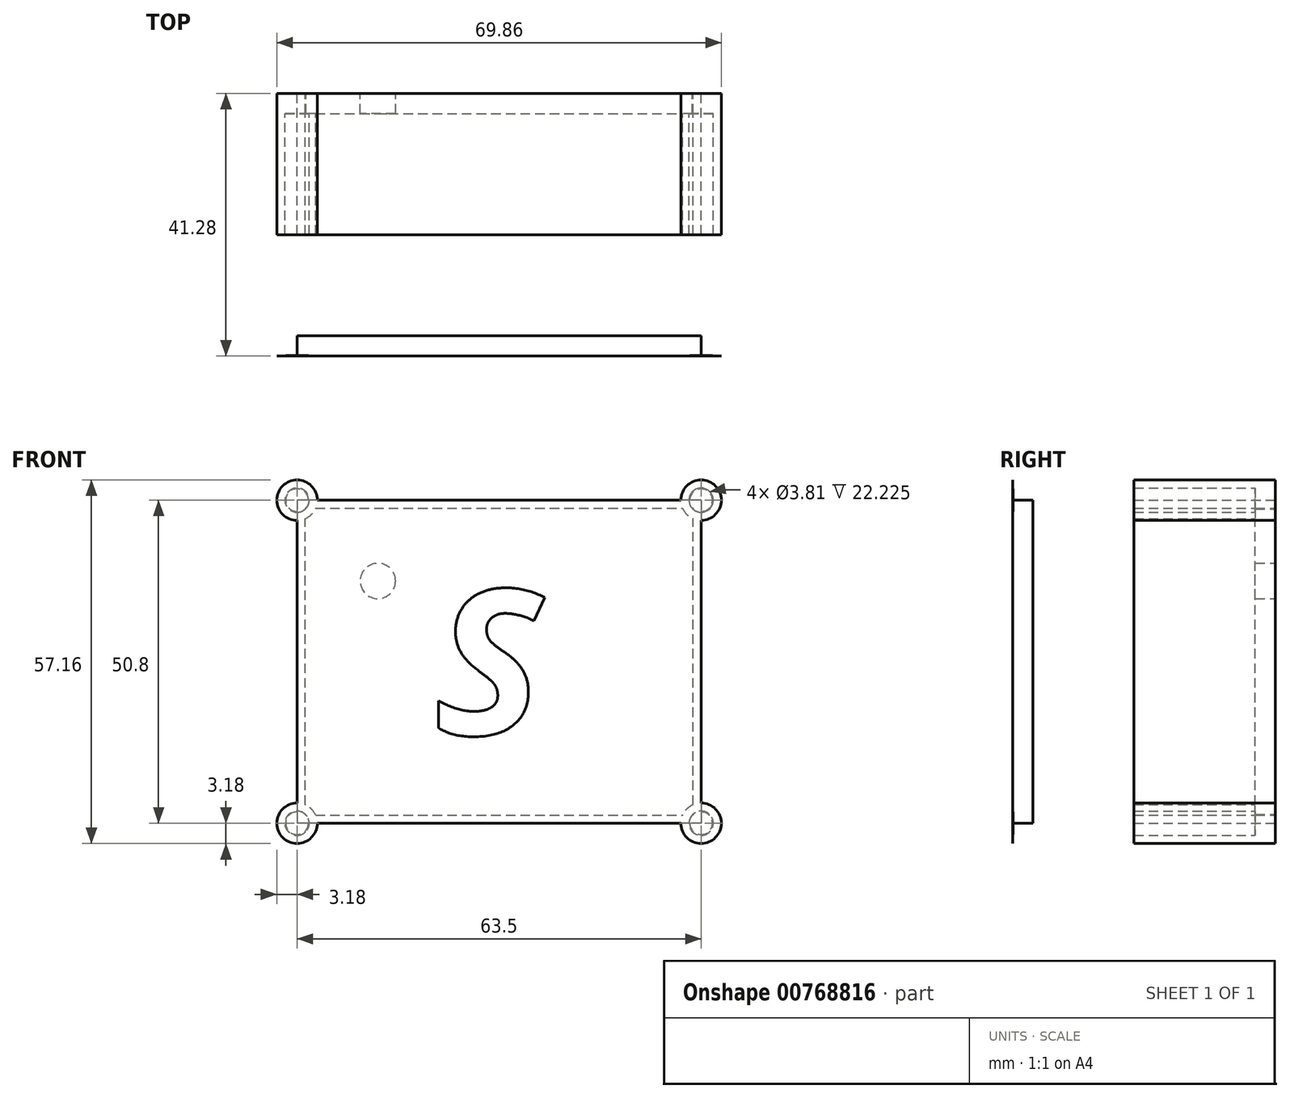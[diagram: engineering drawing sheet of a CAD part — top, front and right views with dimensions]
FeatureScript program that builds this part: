
annotation { "Feature Type Name" : "Feature", "Feature Type Description" : "" }
export const myFeature = defineFeature(function(context is Context, id is Id, definition is map)
    precondition{}
    {
        {
            var Q0;
            Q0=qCreatedBy(makeId("Front.planeOp"),FACE);
            var sketch = newSketch(context, id + "F0", { "sketchPlane" : qUnion([Q0])});
            skLineSegment(sketch, "E0.bottom", {"start": v(31.75, 25.4) * mm, "end": v(-31.75, 25.4) * mm});
            skLineSegment(sketch, "E0.top", {"start": v(31.75, -25.4) * mm, "end": v(-31.75, -25.4) * mm});
            skLineSegment(sketch, "E0.left", {"start": v(31.75, 25.4) * mm, "end": v(31.75, -25.4) * mm});
            skLineSegment(sketch, "E0.right", {"start": v(-31.75, 25.4) * mm, "end": v(-31.75, -25.4) * mm});
            skPoint(sketch, "E0.middle", {"position": v(0, 0) * mm});
            skCircle(sketch, "E1", {"center": v(-19.05, 12.7) * mm, "radius": 2.78 * mm});
            skPoint(sketch, "E2.middle", {"position": v(-31.75, 25.4) * mm});
            skLineSegment(sketch, "E3.bottom", {"start": v(-31.75, 25.4) * mm, "end": v(-19.05, 25.4) * mm, "construction": true});
            skLineSegment(sketch, "E3.top", {"start": v(-31.75, 12.7) * mm, "end": v(-19.05, 12.7) * mm, "construction": true});
            skLineSegment(sketch, "E3.left", {"start": v(-31.75, 25.4) * mm, "end": v(-31.75, 12.7) * mm, "construction": true});
            skLineSegment(sketch, "E3.right", {"start": v(-19.05, 25.4) * mm, "end": v(-19.05, 12.7) * mm, "construction": true});
            skCircle(sketch, "E4", {"center": v(-31.75, 25.4) * mm, "radius": 3.18 * mm});
            skCircle(sketch, "E5", {"center": v(31.75, 25.4) * mm, "radius": 3.18 * mm});
            skCircle(sketch, "E6", {"center": v(31.75, -25.4) * mm, "radius": 3.18 * mm});
            skCircle(sketch, "E7", {"center": v(-31.75, -25.4) * mm, "radius": 3.18 * mm});
            skCircle(sketch, "E8.0", {"center": v(-31.75, 25.4) * mm, "radius": 1.9 * mm});
            skCircle(sketch, "E9.0", {"center": v(31.75, 25.4) * mm, "radius": 1.9 * mm});
            skCircle(sketch, "E10.0", {"center": v(31.75, -25.4) * mm, "radius": 1.9 * mm});
            skCircle(sketch, "E11.0", {"center": v(-31.75, -25.4) * mm, "radius": 1.9 * mm});
            skLineSegment(sketch, "E12.0", {"start": v(30.48, 24.13) * mm, "end": v(-30.48, 24.13) * mm});
            skLineSegment(sketch, "E12.1", {"start": v(30.48, 24.13) * mm, "end": v(30.48, -24.13) * mm});
            skLineSegment(sketch, "E12.2", {"start": v(30.48, -24.13) * mm, "end": v(-30.48, -24.13) * mm});
            skLineSegment(sketch, "E12.3", {"start": v(-30.48, 24.13) * mm, "end": v(-30.48, -24.13) * mm});
            skSolve(sketch);
        }
        {
            var Q0;
            Q0=makeQuery(id+"F0.imprint","IMPRINT",FACE,{"disambiguationData":[TD([[makeQuery(id+"F0.imprint","IMPRINT",EDGE,{"derivedFrom":sQuery(id+"F0.wireOp",EDGE,"E1")}),-1.0]])]});
            var Q1;
            {var subQ0=sQuery(id+"F0.wireOp",EDGE,"E4");var subQ1=sQuery(id+"F0.wireOp",EDGE,"E0.right");var subQ2=makeQuery(id+"F0.imprint","INTERSECT",VERTEX,{"derivedFrom":[subQ1,subQ0]});Q1=makeQuery(id+"F0.imprint","IMPRINT",FACE,{"disambiguationData":[TD([[makeQuery(id+"F0.imprint","IMPRINT",EDGE,{"disambiguationData":[TD([[subQ2,-1.0]])],"derivedFrom":subQ1}),1.0]])]});}
            var Q2;
            Q2=qSketchRegion(id+"F0",true);
            var Q3;
            {var subQ0=sQuery(id+"F0.wireOp",EDGE,"E12.3");var subQ1=sQuery(id+"F0.wireOp",EDGE,"E4");var subQ2=makeQuery(id+"F0.imprint","INTERSECT",VERTEX,{"derivedFrom":[subQ1,subQ0]});Q3=makeQuery(id+"F0.imprint","IMPRINT",FACE,{"disambiguationData":[TD([[makeQuery(id+"F0.imprint","IMPRINT",EDGE,{"disambiguationData":[TD([[subQ2,-1.0]])],"derivedFrom":subQ1}),1.0]])]});}
            var Q4;
            {var subQ0=sQuery(id+"F0.wireOp",EDGE,"E12.2");var subQ1=sQuery(id+"F0.wireOp",EDGE,"E7");var subQ2=makeQuery(id+"F0.imprint","INTERSECT",VERTEX,{"derivedFrom":[subQ1,subQ0]});Q4=makeQuery(id+"F0.imprint","IMPRINT",FACE,{"disambiguationData":[TD([[makeQuery(id+"F0.imprint","IMPRINT",EDGE,{"disambiguationData":[TD([[subQ2,-1.0]])],"derivedFrom":subQ1}),1.0]])]});}
            var Q5;
            {var subQ0=sQuery(id+"F0.wireOp",EDGE,"E12.1");var subQ1=sQuery(id+"F0.wireOp",EDGE,"E6");var subQ2=makeQuery(id+"F0.imprint","INTERSECT",VERTEX,{"derivedFrom":[subQ1,subQ0]});Q5=makeQuery(id+"F0.imprint","IMPRINT",FACE,{"disambiguationData":[TD([[makeQuery(id+"F0.imprint","IMPRINT",EDGE,{"disambiguationData":[TD([[subQ2,-1.0]])],"derivedFrom":subQ1}),1.0]])]});}
            var Q6;
            {var subQ0=sQuery(id+"F0.wireOp",EDGE,"E12.0");var subQ1=sQuery(id+"F0.wireOp",EDGE,"E5");var subQ2=makeQuery(id+"F0.imprint","INTERSECT",VERTEX,{"derivedFrom":[subQ1,subQ0]});Q6=makeQuery(id+"F0.imprint","IMPRINT",FACE,{"disambiguationData":[TD([[makeQuery(id+"F0.imprint","IMPRINT",EDGE,{"disambiguationData":[TD([[subQ2,-1.0]])],"derivedFrom":subQ1}),1.0]])]});}
            var Q7;
            {var subQ1=sQuery(id+"F0.wireOp",EDGE,"E0.right");var subQ5=sQuery(id+"F0.wireOp",EDGE,"E0.bottom");var subQ9=makeQuery(id+"F0.imprint","INTERSECT",VERTEX,{"derivedFrom":[subQ5,subQ1]});Q7=makeQuery(id+"F0.imprint","IMPRINT",FACE,{"disambiguationData":[TD([[makeQuery(id+"F0.imprint","IMPRINT",EDGE,{"disambiguationData":[TD([[subQ9,1.0]])],"derivedFrom":subQ5}),1.0]])]});}
            var Q8;
            {var subQ0=sQuery(id+"F0.wireOp",EDGE,"E0.right");var subQ1=sQuery(id+"F0.wireOp",EDGE,"E0.bottom");var subQ2=makeQuery(id+"F0.imprint","INTERSECT",VERTEX,{"derivedFrom":[subQ1,subQ0]});Q8=makeQuery(id+"F0.imprint","IMPRINT",FACE,{"disambiguationData":[TD([[makeQuery(id+"F0.imprint","IMPRINT",EDGE,{"disambiguationData":[TD([[subQ2,1.0]])],"derivedFrom":subQ1}),-1.0]])]});}
            var Q9;
            {var subQ0=sQuery(id+"F0.wireOp",EDGE,"E0.left");var subQ1=sQuery(id+"F0.wireOp",EDGE,"E0.bottom");var subQ2=makeQuery(id+"F0.imprint","INTERSECT",VERTEX,{"derivedFrom":[subQ1,subQ0]});Q9=makeQuery(id+"F0.imprint","IMPRINT",FACE,{"disambiguationData":[TD([[makeQuery(id+"F0.imprint","IMPRINT",EDGE,{"disambiguationData":[TD([[subQ2,-1.0]])],"derivedFrom":subQ1}),-1.0]])]});}
            var Q10;
            {var subQ1=sQuery(id+"F0.wireOp",EDGE,"E0.left");var subQ5=sQuery(id+"F0.wireOp",EDGE,"E0.bottom");var subQ6=makeQuery(id+"F0.imprint","INTERSECT",VERTEX,{"derivedFrom":[subQ5,subQ1]});Q10=makeQuery(id+"F0.imprint","IMPRINT",FACE,{"disambiguationData":[TD([[makeQuery(id+"F0.imprint","IMPRINT",EDGE,{"disambiguationData":[TD([[subQ6,-1.0]])],"derivedFrom":subQ5}),1.0]])]});}
            var Q11;
            {var subQ0=sQuery(id+"F0.wireOp",EDGE,"E0.left");var subQ1=sQuery(id+"F0.wireOp",EDGE,"E0.top");var subQ2=makeQuery(id+"F0.imprint","INTERSECT",VERTEX,{"derivedFrom":[subQ1,subQ0]});Q11=makeQuery(id+"F0.imprint","IMPRINT",FACE,{"disambiguationData":[TD([[makeQuery(id+"F0.imprint","IMPRINT",EDGE,{"disambiguationData":[TD([[subQ2,-1.0]])],"derivedFrom":subQ1}),1.0]])]});}
            var Q12;
            {var subQ1=sQuery(id+"F0.wireOp",EDGE,"E0.top");var subQ5=sQuery(id+"F0.wireOp",EDGE,"E0.left");var subQ6=makeQuery(id+"F0.imprint","INTERSECT",VERTEX,{"derivedFrom":[subQ1,subQ5]});Q12=makeQuery(id+"F0.imprint","IMPRINT",FACE,{"disambiguationData":[TD([[makeQuery(id+"F0.imprint","IMPRINT",EDGE,{"disambiguationData":[TD([[subQ6,-1.0]])],"derivedFrom":subQ1}),-1.0]])]});}
            var Q13;
            {var subQ1=sQuery(id+"F0.wireOp",EDGE,"E0.right");var subQ5=sQuery(id+"F0.wireOp",EDGE,"E0.top");var subQ9=makeQuery(id+"F0.imprint","INTERSECT",VERTEX,{"derivedFrom":[subQ5,subQ1]});Q13=makeQuery(id+"F0.imprint","IMPRINT",FACE,{"disambiguationData":[TD([[makeQuery(id+"F0.imprint","IMPRINT",EDGE,{"disambiguationData":[TD([[subQ9,1.0]])],"derivedFrom":subQ5}),-1.0]])]});}
            var Q14;
            {var subQ0=sQuery(id+"F0.wireOp",EDGE,"E0.right");var subQ1=sQuery(id+"F0.wireOp",EDGE,"E0.top");var subQ2=makeQuery(id+"F0.imprint","INTERSECT",VERTEX,{"derivedFrom":[subQ1,subQ0]});Q14=makeQuery(id+"F0.imprint","IMPRINT",FACE,{"disambiguationData":[TD([[makeQuery(id+"F0.imprint","IMPRINT",EDGE,{"disambiguationData":[TD([[subQ2,1.0]])],"derivedFrom":subQ1}),1.0]])]});}
            extrude(context, id + "F1", {"entities" : qUnion([Q0, Q1, Q2, Q3, Q4, Q5, Q6, Q7, Q8, Q9, Q10, Q11, Q12, Q13, Q14]), "depth" : 3.17 * mm, "offsetDistance" : 25.4 * mm});
        }
        {
            var Q0;
            {var subQ0=sQuery(id+"F0.wireOp",EDGE,"E4");var subQ1=sQuery(id+"F0.wireOp",EDGE,"E0.right");var subQ2=makeQuery(id+"F0.imprint","INTERSECT",VERTEX,{"derivedFrom":[subQ1,subQ0]});Q0=makeQuery(id+"F0.imprint","IMPRINT",FACE,{"disambiguationData":[TD([[makeQuery(id+"F0.imprint","IMPRINT",EDGE,{"disambiguationData":[TD([[subQ2,-1.0]])],"derivedFrom":subQ1}),1.0]])]});}
            var Q1;
            {var subQ0=sQuery(id+"F0.wireOp",EDGE,"E6");var subQ1=sQuery(id+"F0.wireOp",EDGE,"E0.top");var subQ2=makeQuery(id+"F0.imprint","INTERSECT",VERTEX,{"derivedFrom":[subQ1,subQ0]});Q1=makeQuery(id+"F0.imprint","IMPRINT",FACE,{"disambiguationData":[TD([[makeQuery(id+"F0.imprint","IMPRINT",EDGE,{"disambiguationData":[TD([[subQ2,-1.0]])],"derivedFrom":subQ1}),-1.0]])]});}
            var Q2;
            {var subQ0=sQuery(id+"F0.wireOp",EDGE,"E5");var subQ1=sQuery(id+"F0.wireOp",EDGE,"E0.left");var subQ2=makeQuery(id+"F0.imprint","INTERSECT",VERTEX,{"derivedFrom":[subQ1,subQ0]});Q2=makeQuery(id+"F0.imprint","IMPRINT",FACE,{"disambiguationData":[TD([[makeQuery(id+"F0.imprint","IMPRINT",EDGE,{"disambiguationData":[TD([[subQ2,-1.0]])],"derivedFrom":subQ1}),-1.0]])]});}
            var Q3;
            {var subQ0=sQuery(id+"F0.wireOp",EDGE,"E5");var subQ1=sQuery(id+"F0.wireOp",EDGE,"E0.bottom");var subQ2=makeQuery(id+"F0.imprint","INTERSECT",VERTEX,{"derivedFrom":[subQ1,subQ0]});Q3=makeQuery(id+"F0.imprint","IMPRINT",FACE,{"disambiguationData":[TD([[makeQuery(id+"F0.imprint","IMPRINT",EDGE,{"disambiguationData":[TD([[subQ2,-1.0]])],"derivedFrom":subQ1}),1.0]])]});}
            var Q4;
            {var subQ0=sQuery(id+"F0.wireOp",EDGE,"E12.0");var subQ1=sQuery(id+"F0.wireOp",EDGE,"E5");var subQ2=makeQuery(id+"F0.imprint","INTERSECT",VERTEX,{"derivedFrom":[subQ1,subQ0]});Q4=makeQuery(id+"F0.imprint","IMPRINT",FACE,{"disambiguationData":[TD([[makeQuery(id+"F0.imprint","IMPRINT",EDGE,{"disambiguationData":[TD([[subQ2,-1.0]])],"derivedFrom":subQ1}),1.0]])]});}
            var Q5;
            {var subQ0=sQuery(id+"F0.wireOp",EDGE,"E5");var subQ1=sQuery(id+"F0.wireOp",EDGE,"E0.left");var subQ2=makeQuery(id+"F0.imprint","INTERSECT",VERTEX,{"derivedFrom":[subQ1,subQ0]});Q5=makeQuery(id+"F0.imprint","IMPRINT",FACE,{"disambiguationData":[TD([[makeQuery(id+"F0.imprint","IMPRINT",EDGE,{"disambiguationData":[TD([[subQ2,1.0]])],"derivedFrom":subQ1}),-1.0]])]});}
            var Q6;
            {var subQ0=sQuery(id+"F0.wireOp",EDGE,"E5");var subQ1=sQuery(id+"F0.wireOp",EDGE,"E0.bottom");var subQ2=makeQuery(id+"F0.imprint","INTERSECT",VERTEX,{"derivedFrom":[subQ1,subQ0]});Q6=makeQuery(id+"F0.imprint","IMPRINT",FACE,{"disambiguationData":[TD([[makeQuery(id+"F0.imprint","IMPRINT",EDGE,{"disambiguationData":[TD([[subQ2,1.0]])],"derivedFrom":subQ1}),1.0]])]});}
            var Q7;
            {var subQ0=sQuery(id+"F0.wireOp",EDGE,"E5");var subQ1=sQuery(id+"F0.wireOp",EDGE,"E0.bottom");var subQ2=makeQuery(id+"F0.imprint","INTERSECT",VERTEX,{"derivedFrom":[subQ1,subQ0]});Q7=makeQuery(id+"F0.imprint","IMPRINT",FACE,{"disambiguationData":[TD([[makeQuery(id+"F0.imprint","IMPRINT",EDGE,{"disambiguationData":[TD([[subQ2,1.0]])],"derivedFrom":subQ1}),-1.0]])]});}
            var Q8;
            {var subQ0=sQuery(id+"F0.wireOp",EDGE,"E12.1");var subQ1=sQuery(id+"F0.wireOp",EDGE,"E6");var subQ2=makeQuery(id+"F0.imprint","INTERSECT",VERTEX,{"derivedFrom":[subQ1,subQ0]});Q8=makeQuery(id+"F0.imprint","IMPRINT",FACE,{"disambiguationData":[TD([[makeQuery(id+"F0.imprint","IMPRINT",EDGE,{"disambiguationData":[TD([[subQ2,-1.0]])],"derivedFrom":subQ1}),1.0]])]});}
            var Q9;
            {var subQ0=sQuery(id+"F0.wireOp",EDGE,"E6");var subQ1=sQuery(id+"F0.wireOp",EDGE,"E0.top");var subQ2=makeQuery(id+"F0.imprint","INTERSECT",VERTEX,{"derivedFrom":[subQ1,subQ0]});Q9=makeQuery(id+"F0.imprint","IMPRINT",FACE,{"disambiguationData":[TD([[makeQuery(id+"F0.imprint","IMPRINT",EDGE,{"disambiguationData":[TD([[subQ2,1.0]])],"derivedFrom":subQ1}),-1.0]])]});}
            var Q10;
            {var subQ0=sQuery(id+"F0.wireOp",EDGE,"E6");var subQ1=sQuery(id+"F0.wireOp",EDGE,"E0.left");var subQ2=makeQuery(id+"F0.imprint","INTERSECT",VERTEX,{"derivedFrom":[subQ1,subQ0]});Q10=makeQuery(id+"F0.imprint","IMPRINT",FACE,{"disambiguationData":[TD([[makeQuery(id+"F0.imprint","IMPRINT",EDGE,{"disambiguationData":[TD([[subQ2,-1.0]])],"derivedFrom":subQ1}),-1.0]])]});}
            var Q11;
            {var subQ0=sQuery(id+"F0.wireOp",EDGE,"E6");var subQ1=sQuery(id+"F0.wireOp",EDGE,"E0.top");var subQ2=makeQuery(id+"F0.imprint","INTERSECT",VERTEX,{"derivedFrom":[subQ1,subQ0]});Q11=makeQuery(id+"F0.imprint","IMPRINT",FACE,{"disambiguationData":[TD([[makeQuery(id+"F0.imprint","IMPRINT",EDGE,{"disambiguationData":[TD([[subQ2,1.0]])],"derivedFrom":subQ1}),1.0]])]});}
            var Q12;
            {var subQ0=sQuery(id+"F0.wireOp",EDGE,"E7");var subQ1=sQuery(id+"F0.wireOp",EDGE,"E0.top");var subQ2=makeQuery(id+"F0.imprint","INTERSECT",VERTEX,{"derivedFrom":[subQ1,subQ0]});Q12=makeQuery(id+"F0.imprint","IMPRINT",FACE,{"disambiguationData":[TD([[makeQuery(id+"F0.imprint","IMPRINT",EDGE,{"disambiguationData":[TD([[subQ2,-1.0]])],"derivedFrom":subQ1}),1.0]])]});}
            var Q13;
            {var subQ0=sQuery(id+"F0.wireOp",EDGE,"E7");var subQ1=sQuery(id+"F0.wireOp",EDGE,"E0.right");var subQ2=makeQuery(id+"F0.imprint","INTERSECT",VERTEX,{"derivedFrom":[subQ1,subQ0]});Q13=makeQuery(id+"F0.imprint","IMPRINT",FACE,{"disambiguationData":[TD([[makeQuery(id+"F0.imprint","IMPRINT",EDGE,{"disambiguationData":[TD([[subQ2,-1.0]])],"derivedFrom":subQ1}),1.0]])]});}
            var Q14;
            {var subQ0=sQuery(id+"F0.wireOp",EDGE,"E12.2");var subQ1=sQuery(id+"F0.wireOp",EDGE,"E7");var subQ2=makeQuery(id+"F0.imprint","INTERSECT",VERTEX,{"derivedFrom":[subQ1,subQ0]});Q14=makeQuery(id+"F0.imprint","IMPRINT",FACE,{"disambiguationData":[TD([[makeQuery(id+"F0.imprint","IMPRINT",EDGE,{"disambiguationData":[TD([[subQ2,-1.0]])],"derivedFrom":subQ1}),1.0]])]});}
            var Q15;
            {var subQ0=sQuery(id+"F0.wireOp",EDGE,"E7");var subQ1=sQuery(id+"F0.wireOp",EDGE,"E0.top");var subQ2=makeQuery(id+"F0.imprint","INTERSECT",VERTEX,{"derivedFrom":[subQ1,subQ0]});Q15=makeQuery(id+"F0.imprint","IMPRINT",FACE,{"disambiguationData":[TD([[makeQuery(id+"F0.imprint","IMPRINT",EDGE,{"disambiguationData":[TD([[subQ2,-1.0]])],"derivedFrom":subQ1}),-1.0]])]});}
            var Q16;
            {var subQ0=sQuery(id+"F0.wireOp",EDGE,"E4");var subQ1=sQuery(id+"F0.wireOp",EDGE,"E0.bottom");var subQ2=makeQuery(id+"F0.imprint","INTERSECT",VERTEX,{"derivedFrom":[subQ1,subQ0]});Q16=makeQuery(id+"F0.imprint","IMPRINT",FACE,{"disambiguationData":[TD([[makeQuery(id+"F0.imprint","IMPRINT",EDGE,{"disambiguationData":[TD([[subQ2,-1.0]])],"derivedFrom":subQ1}),1.0]])]});}
            var Q17;
            {var subQ0=sQuery(id+"F0.wireOp",EDGE,"E12.3");var subQ1=sQuery(id+"F0.wireOp",EDGE,"E4");var subQ2=makeQuery(id+"F0.imprint","INTERSECT",VERTEX,{"derivedFrom":[subQ1,subQ0]});Q17=makeQuery(id+"F0.imprint","IMPRINT",FACE,{"disambiguationData":[TD([[makeQuery(id+"F0.imprint","IMPRINT",EDGE,{"disambiguationData":[TD([[subQ2,-1.0]])],"derivedFrom":subQ1}),1.0]])]});}
            var Q18;
            {var subQ0=sQuery(id+"F0.wireOp",EDGE,"E4");var subQ1=sQuery(id+"F0.wireOp",EDGE,"E0.right");var subQ2=makeQuery(id+"F0.imprint","INTERSECT",VERTEX,{"derivedFrom":[subQ1,subQ0]});Q18=makeQuery(id+"F0.imprint","IMPRINT",FACE,{"disambiguationData":[TD([[makeQuery(id+"F0.imprint","IMPRINT",EDGE,{"disambiguationData":[TD([[subQ2,1.0]])],"derivedFrom":subQ1}),1.0]])]});}
            var Q19;
            {var subQ0=sQuery(id+"F0.wireOp",EDGE,"E4");var subQ1=sQuery(id+"F0.wireOp",EDGE,"E0.bottom");var subQ2=makeQuery(id+"F0.imprint","INTERSECT",VERTEX,{"derivedFrom":[subQ1,subQ0]});Q19=makeQuery(id+"F0.imprint","IMPRINT",FACE,{"disambiguationData":[TD([[makeQuery(id+"F0.imprint","IMPRINT",EDGE,{"disambiguationData":[TD([[subQ2,-1.0]])],"derivedFrom":subQ1}),-1.0]])]});}
            extrude(context, id + "F2", {"entities" : qUnion([Q0, Q1, Q2, Q3, Q4, Q5, Q6, Q7, Q8, Q9, Q10, Q11, Q12, Q13, Q14, Q15, Q16, Q17, Q18, Q19]), "operationType" : NewBodyOperationType.ADD, "depth" : 22.22 * mm, "offsetDistance" : 25.4 * mm});
        }
        {
            var Q0;
            Q0=qCreatedBy(makeId("Right.planeOp"),FACE);
            var sketch = newSketch(context, id + "F3", { "sketchPlane" : qUnion([Q0])});
            skLineSegment(sketch, "E13.bottom", {"start": v(-38.1, 25.4) * mm, "end": v(38.1, 25.4) * mm, "construction": true});
            skLineSegment(sketch, "E13.top", {"start": v(-38.1, -25.4) * mm, "end": v(38.1, -25.4) * mm, "construction": true});
            skLineSegment(sketch, "E13.left", {"start": v(-38.1, 25.4) * mm, "end": v(-38.1, -25.4) * mm, "construction": true});
            skLineSegment(sketch, "E13.right", {"start": v(38.1, 25.4) * mm, "end": v(38.1, -25.4) * mm, "construction": true});
            skPoint(sketch, "E13.middle", {"position": v(0, 0) * mm});
            skLineSegment(sketch, "E14.bottom", {"start": v(-38.1, 25.4) * mm, "end": v(-41.28, 25.4) * mm});
            skLineSegment(sketch, "E14.top", {"start": v(-38.1, -25.4) * mm, "end": v(-41.27, -25.4) * mm});
            skLineSegment(sketch, "E14.left", {"start": v(-38.1, 25.4) * mm, "end": v(-38.1, -25.4) * mm});
            skLineSegment(sketch, "E14.right", {"start": v(-41.28, 25.4) * mm, "end": v(-41.27, -25.4) * mm});
            skSolve(sketch);
        }
        {
            var Q0;
            Q0=makeQuery(id+"F3.imprint","IMPRINT",FACE,{"disambiguationData":[TD([[makeQuery(id+"F3.imprint","IMPRINT",EDGE,{"derivedFrom":sQuery(id+"F3.wireOp",EDGE,"E14.bottom")}),1.0]])]});
            extrude(context, id + "F4", {"entities" : qUnion([Q0]), "endBound" : BoundingType.SYMMETRIC, "depth" : 63.5 * mm, "offsetDistance" : 25.4 * mm});
        }
        {
            var Q0;
            Q0=makeQuery(id+"F4.opExtrude","SWEPT_FACE",FACE,{"disambiguationData":[OSD([sQuery(id+"F3.wireOp",EDGE,"E14.right")])]});
            var sketch = newSketch(context, id + "F5", { "sketchPlane" : qUnion([Q0])});
            skCircle(sketch, "E15", {"center": v(-31.75, 25.4) * mm, "radius": 3.18 * mm});
            skCircle(sketch, "E16", {"center": v(31.75, 25.4) * mm, "radius": 3.18 * mm});
            skCircle(sketch, "E17", {"center": v(31.75, -25.4) * mm, "radius": 3.18 * mm});
            skCircle(sketch, "E18", {"center": v(-31.75, -25.4) * mm, "radius": 3.18 * mm});
            skCircle(sketch, "E19.0", {"center": v(31.75, 25.4) * mm, "radius": 1.78 * mm});
            skCircle(sketch, "E20.0", {"center": v(-31.75, 25.4) * mm, "radius": 1.78 * mm});
            skCircle(sketch, "E21.0", {"center": v(-31.75, -25.4) * mm, "radius": 1.78 * mm});
            skCircle(sketch, "E22.0", {"center": v(31.75, -25.4) * mm, "radius": 1.78 * mm});
            skText(sketch, "E23", { "text": "S", "fontName": "OpenSans-BoldItalic.ttf"});
            const initialGuessF5  = {"E23": [-0.01014, -0.01149, 1, 0, 0.02298]};
            skSetInitialGuess(sketch, initialGuessF5);
            skSolve(sketch);
        }
        {
            var Q0;
            {var subQ0=sQuery(id+"F5.wireOp",EDGE,"E16");var subQ1=sQuery(id+"F3.wireOp",EDGE,"E14.right");var subQ4=makeQuery(id+"F4.opExtrude","CAP_EDGE",EDGE,{"disambiguationData":[OSD([subQ1])],"isStart":false});var subQ5=makeQuery(id+"F5.imprint","INTERSECT",VERTEX,{"derivedFrom":[subQ4,subQ0]});Q0=makeQuery(id+"F5.imprint","IMPRINT",FACE,{"disambiguationData":[TD([[makeQuery(id+"F5.imprint","IMPRINT",EDGE,{"disambiguationData":[TD([[subQ5,1.0]])],"derivedFrom":subQ4}),1.0]])]});}
            var Q1;
            {var subQ0=sQuery(id+"F5.wireOp",EDGE,"E19.0");var subQ1=sQuery(id+"F3.wireOp",EDGE,"E14.right");var subQ4=makeQuery(id+"F4.opExtrude","CAP_EDGE",EDGE,{"disambiguationData":[OSD([subQ1])],"isStart":false});var subQ5=makeQuery(id+"F5.imprint","INTERSECT",VERTEX,{"derivedFrom":[subQ4,subQ0]});Q1=makeQuery(id+"F5.imprint","IMPRINT",FACE,{"disambiguationData":[TD([[makeQuery(id+"F5.imprint","IMPRINT",EDGE,{"disambiguationData":[TD([[subQ5,-1.0]])],"derivedFrom":subQ0}),1.0]])]});}
            var Q2;
            {var subQ0=sQuery(id+"F5.wireOp",EDGE,"E17");var subQ1=sQuery(id+"F3.wireOp",EDGE,"E14.right");var subQ4=makeQuery(id+"F4.opExtrude","CAP_EDGE",EDGE,{"disambiguationData":[OSD([subQ1])],"isStart":false});var subQ5=makeQuery(id+"F5.imprint","INTERSECT",VERTEX,{"derivedFrom":[subQ4,subQ0]});Q2=makeQuery(id+"F5.imprint","IMPRINT",FACE,{"disambiguationData":[TD([[makeQuery(id+"F5.imprint","IMPRINT",EDGE,{"disambiguationData":[TD([[subQ5,-1.0]])],"derivedFrom":subQ4}),1.0]])]});}
            var Q3;
            {var subQ0=sQuery(id+"F5.wireOp",EDGE,"E22.0");var subQ1=sQuery(id+"F3.wireOp",EDGE,"E14.right");var subQ4=makeQuery(id+"F4.opExtrude","CAP_EDGE",EDGE,{"disambiguationData":[OSD([subQ1])],"isStart":false});var subQ5=makeQuery(id+"F5.imprint","INTERSECT",VERTEX,{"derivedFrom":[subQ4,subQ0]});Q3=makeQuery(id+"F5.imprint","IMPRINT",FACE,{"disambiguationData":[TD([[makeQuery(id+"F5.imprint","IMPRINT",EDGE,{"disambiguationData":[TD([[subQ5,1.0]])],"derivedFrom":subQ0}),1.0]])]});}
            var Q4;
            {var subQ0=sQuery(id+"F5.wireOp",EDGE,"E18");var subQ1=sQuery(id+"F3.wireOp",EDGE,"E14.right");var subQ4=makeQuery(id+"F4.opExtrude","CAP_EDGE",EDGE,{"disambiguationData":[OSD([subQ1])],"isStart":true});var subQ5=makeQuery(id+"F5.imprint","INTERSECT",VERTEX,{"derivedFrom":[subQ4,subQ0]});Q4=makeQuery(id+"F5.imprint","IMPRINT",FACE,{"disambiguationData":[TD([[makeQuery(id+"F5.imprint","IMPRINT",EDGE,{"disambiguationData":[TD([[subQ5,-1.0]])],"derivedFrom":subQ4}),-1.0]])]});}
            var Q5;
            {var subQ0=sQuery(id+"F5.wireOp",EDGE,"E21.0");var subQ1=sQuery(id+"F3.wireOp",EDGE,"E14.right");var subQ4=makeQuery(id+"F4.opExtrude","CAP_EDGE",EDGE,{"disambiguationData":[OSD([subQ1])],"isStart":true});var subQ5=makeQuery(id+"F5.imprint","INTERSECT",VERTEX,{"derivedFrom":[subQ4,subQ0]});Q5=makeQuery(id+"F5.imprint","IMPRINT",FACE,{"disambiguationData":[TD([[makeQuery(id+"F5.imprint","IMPRINT",EDGE,{"disambiguationData":[TD([[subQ5,-1.0]])],"derivedFrom":subQ0}),1.0]])]});}
            var Q6;
            {var subQ0=sQuery(id+"F5.wireOp",EDGE,"E21.0");var subQ1=sQuery(id+"F3.wireOp",EDGE,"E14.right");var subQ4=makeQuery(id+"F4.opExtrude","CAP_EDGE",EDGE,{"disambiguationData":[OSD([subQ1])],"isStart":true});var subQ5=makeQuery(id+"F5.imprint","INTERSECT",VERTEX,{"derivedFrom":[subQ4,subQ0]});Q6=makeQuery(id+"F5.imprint","IMPRINT",FACE,{"disambiguationData":[TD([[makeQuery(id+"F5.imprint","IMPRINT",EDGE,{"disambiguationData":[TD([[subQ5,1.0]])],"derivedFrom":subQ0}),1.0]])]});}
            var Q7;
            {var subQ0=sQuery(id+"F5.wireOp",EDGE,"E18");var subQ1=sQuery(id+"F3.wireOp",EDGE,"E14.right");var subQ4=makeQuery(id+"F4.opExtrude","CAP_EDGE",EDGE,{"disambiguationData":[OSD([subQ1])],"isStart":true});var subQ5=makeQuery(id+"F5.imprint","INTERSECT",VERTEX,{"derivedFrom":[subQ4,subQ0]});Q7=makeQuery(id+"F5.imprint","IMPRINT",FACE,{"disambiguationData":[TD([[makeQuery(id+"F5.imprint","IMPRINT",EDGE,{"disambiguationData":[TD([[subQ5,-1.0]])],"derivedFrom":subQ4}),1.0]])]});}
            var Q8;
            {var subQ0=sQuery(id+"F5.wireOp",EDGE,"E17");var subQ1=sQuery(id+"F3.wireOp",EDGE,"E14.right");var subQ4=makeQuery(id+"F4.opExtrude","CAP_EDGE",EDGE,{"disambiguationData":[OSD([subQ1])],"isStart":false});var subQ5=makeQuery(id+"F5.imprint","INTERSECT",VERTEX,{"derivedFrom":[subQ4,subQ0]});Q8=makeQuery(id+"F5.imprint","IMPRINT",FACE,{"disambiguationData":[TD([[makeQuery(id+"F5.imprint","IMPRINT",EDGE,{"disambiguationData":[TD([[subQ5,-1.0]])],"derivedFrom":subQ4}),-1.0]])]});}
            var Q9;
            {var subQ0=sQuery(id+"F5.wireOp",EDGE,"E22.0");var subQ1=sQuery(id+"F3.wireOp",EDGE,"E14.right");var subQ4=makeQuery(id+"F4.opExtrude","CAP_EDGE",EDGE,{"disambiguationData":[OSD([subQ1])],"isStart":false});var subQ5=makeQuery(id+"F5.imprint","INTERSECT",VERTEX,{"derivedFrom":[subQ4,subQ0]});Q9=makeQuery(id+"F5.imprint","IMPRINT",FACE,{"disambiguationData":[TD([[makeQuery(id+"F5.imprint","IMPRINT",EDGE,{"disambiguationData":[TD([[subQ5,-1.0]])],"derivedFrom":subQ0}),1.0]])]});}
            var Q10;
            {var subQ0=sQuery(id+"F5.wireOp",EDGE,"E16");var subQ1=sQuery(id+"F3.wireOp",EDGE,"E14.right");var subQ4=makeQuery(id+"F4.opExtrude","CAP_EDGE",EDGE,{"disambiguationData":[OSD([subQ1])],"isStart":false});var subQ5=makeQuery(id+"F5.imprint","INTERSECT",VERTEX,{"derivedFrom":[subQ4,subQ0]});Q10=makeQuery(id+"F5.imprint","IMPRINT",FACE,{"disambiguationData":[TD([[makeQuery(id+"F5.imprint","IMPRINT",EDGE,{"disambiguationData":[TD([[subQ5,1.0]])],"derivedFrom":subQ4}),-1.0]])]});}
            var Q11;
            {var subQ0=sQuery(id+"F5.wireOp",EDGE,"E19.0");var subQ1=sQuery(id+"F3.wireOp",EDGE,"E14.right");var subQ4=makeQuery(id+"F4.opExtrude","CAP_EDGE",EDGE,{"disambiguationData":[OSD([subQ1])],"isStart":false});var subQ5=makeQuery(id+"F5.imprint","INTERSECT",VERTEX,{"derivedFrom":[subQ4,subQ0]});Q11=makeQuery(id+"F5.imprint","IMPRINT",FACE,{"disambiguationData":[TD([[makeQuery(id+"F5.imprint","IMPRINT",EDGE,{"disambiguationData":[TD([[subQ5,1.0]])],"derivedFrom":subQ0}),1.0]])]});}
            var Q12;
            {var subQ0=sQuery(id+"F5.wireOp",EDGE,"E20.0");var subQ1=sQuery(id+"F3.wireOp",EDGE,"E14.right");var subQ4=makeQuery(id+"F4.opExtrude","CAP_EDGE",EDGE,{"disambiguationData":[OSD([subQ1])],"isStart":true});var subQ5=makeQuery(id+"F5.imprint","INTERSECT",VERTEX,{"derivedFrom":[subQ4,subQ0]});Q12=makeQuery(id+"F5.imprint","IMPRINT",FACE,{"disambiguationData":[TD([[makeQuery(id+"F5.imprint","IMPRINT",EDGE,{"disambiguationData":[TD([[subQ5,-1.0]])],"derivedFrom":subQ0}),1.0]])]});}
            var Q13;
            {var subQ0=sQuery(id+"F5.wireOp",EDGE,"E15");var subQ1=sQuery(id+"F3.wireOp",EDGE,"E14.right");var subQ4=makeQuery(id+"F4.opExtrude","CAP_EDGE",EDGE,{"disambiguationData":[OSD([subQ1])],"isStart":true});var subQ5=makeQuery(id+"F5.imprint","INTERSECT",VERTEX,{"derivedFrom":[subQ4,subQ0]});Q13=makeQuery(id+"F5.imprint","IMPRINT",FACE,{"disambiguationData":[TD([[makeQuery(id+"F5.imprint","IMPRINT",EDGE,{"disambiguationData":[TD([[subQ5,1.0]])],"derivedFrom":subQ4}),1.0]])]});}
            var Q14;
            {var subQ0=sQuery(id+"F5.wireOp",EDGE,"E20.0");var subQ1=sQuery(id+"F3.wireOp",EDGE,"E14.right");var subQ4=makeQuery(id+"F4.opExtrude","CAP_EDGE",EDGE,{"disambiguationData":[OSD([subQ1])],"isStart":true});var subQ5=makeQuery(id+"F5.imprint","INTERSECT",VERTEX,{"derivedFrom":[subQ4,subQ0]});Q14=makeQuery(id+"F5.imprint","IMPRINT",FACE,{"disambiguationData":[TD([[makeQuery(id+"F5.imprint","IMPRINT",EDGE,{"disambiguationData":[TD([[subQ5,1.0]])],"derivedFrom":subQ0}),1.0]])]});}
            var Q15;
            {var subQ0=sQuery(id+"F5.wireOp",EDGE,"E15");var subQ1=sQuery(id+"F3.wireOp",EDGE,"E14.right");var subQ4=makeQuery(id+"F4.opExtrude","CAP_EDGE",EDGE,{"disambiguationData":[OSD([subQ1])],"isStart":true});var subQ5=makeQuery(id+"F5.imprint","INTERSECT",VERTEX,{"derivedFrom":[subQ4,subQ0]});Q15=makeQuery(id+"F5.imprint","IMPRINT",FACE,{"disambiguationData":[TD([[makeQuery(id+"F5.imprint","IMPRINT",EDGE,{"disambiguationData":[TD([[subQ5,1.0]])],"derivedFrom":subQ4}),-1.0]])]});}
            extrude(context, id + "F6", {"entities" : qUnion([Q0, Q1, Q2, Q3, Q4, Q5, Q6, Q7, Q8, Q9, Q10, Q11, Q12, Q13, Q14, Q15]), "operationType" : NewBodyOperationType.ADD, "oppositeDirection" : true, "depth" : 1 / 203.2 * mm, "offsetDistance" : 25.4 * mm});
        }
        {
            var Q0;
            {var subQ0=sQuery(id+"F5.wireOp",EDGE,"E20.0");var subQ1=sQuery(id+"F3.wireOp",EDGE,"E14.right");var subQ4=makeQuery(id+"F4.opExtrude","CAP_EDGE",EDGE,{"disambiguationData":[OSD([subQ1])],"isStart":true});var subQ5=makeQuery(id+"F5.imprint","INTERSECT",VERTEX,{"derivedFrom":[subQ4,subQ0]});Q0=makeQuery(id+"F5.imprint","IMPRINT",FACE,{"disambiguationData":[TD([[makeQuery(id+"F5.imprint","IMPRINT",EDGE,{"disambiguationData":[TD([[subQ5,1.0]])],"derivedFrom":subQ0}),1.0]])]});}
            var Q1;
            {var subQ0=sQuery(id+"F5.wireOp",EDGE,"E20.0");var subQ1=sQuery(id+"F3.wireOp",EDGE,"E14.right");var subQ4=makeQuery(id+"F4.opExtrude","CAP_EDGE",EDGE,{"disambiguationData":[OSD([subQ1])],"isStart":true});var subQ5=makeQuery(id+"F5.imprint","INTERSECT",VERTEX,{"derivedFrom":[subQ4,subQ0]});Q1=makeQuery(id+"F5.imprint","IMPRINT",FACE,{"disambiguationData":[TD([[makeQuery(id+"F5.imprint","IMPRINT",EDGE,{"disambiguationData":[TD([[subQ5,-1.0]])],"derivedFrom":subQ0}),1.0]])]});}
            var Q2;
            {var subQ0=sQuery(id+"F5.wireOp",EDGE,"E19.0");var subQ1=sQuery(id+"F3.wireOp",EDGE,"E14.right");var subQ4=makeQuery(id+"F4.opExtrude","CAP_EDGE",EDGE,{"disambiguationData":[OSD([subQ1])],"isStart":false});var subQ5=makeQuery(id+"F5.imprint","INTERSECT",VERTEX,{"derivedFrom":[subQ4,subQ0]});Q2=makeQuery(id+"F5.imprint","IMPRINT",FACE,{"disambiguationData":[TD([[makeQuery(id+"F5.imprint","IMPRINT",EDGE,{"disambiguationData":[TD([[subQ5,-1.0]])],"derivedFrom":subQ0}),1.0]])]});}
            var Q3;
            {var subQ0=sQuery(id+"F5.wireOp",EDGE,"E19.0");var subQ1=sQuery(id+"F3.wireOp",EDGE,"E14.right");var subQ4=makeQuery(id+"F4.opExtrude","CAP_EDGE",EDGE,{"disambiguationData":[OSD([subQ1])],"isStart":false});var subQ5=makeQuery(id+"F5.imprint","INTERSECT",VERTEX,{"derivedFrom":[subQ4,subQ0]});Q3=makeQuery(id+"F5.imprint","IMPRINT",FACE,{"disambiguationData":[TD([[makeQuery(id+"F5.imprint","IMPRINT",EDGE,{"disambiguationData":[TD([[subQ5,1.0]])],"derivedFrom":subQ0}),1.0]])]});}
            var Q4;
            {var subQ0=sQuery(id+"F5.wireOp",EDGE,"E22.0");var subQ1=sQuery(id+"F3.wireOp",EDGE,"E14.right");var subQ4=makeQuery(id+"F4.opExtrude","CAP_EDGE",EDGE,{"disambiguationData":[OSD([subQ1])],"isStart":false});var subQ5=makeQuery(id+"F5.imprint","INTERSECT",VERTEX,{"derivedFrom":[subQ4,subQ0]});Q4=makeQuery(id+"F5.imprint","IMPRINT",FACE,{"disambiguationData":[TD([[makeQuery(id+"F5.imprint","IMPRINT",EDGE,{"disambiguationData":[TD([[subQ5,1.0]])],"derivedFrom":subQ0}),1.0]])]});}
            var Q5;
            {var subQ0=sQuery(id+"F5.wireOp",EDGE,"E22.0");var subQ1=sQuery(id+"F3.wireOp",EDGE,"E14.right");var subQ4=makeQuery(id+"F4.opExtrude","CAP_EDGE",EDGE,{"disambiguationData":[OSD([subQ1])],"isStart":false});var subQ5=makeQuery(id+"F5.imprint","INTERSECT",VERTEX,{"derivedFrom":[subQ4,subQ0]});Q5=makeQuery(id+"F5.imprint","IMPRINT",FACE,{"disambiguationData":[TD([[makeQuery(id+"F5.imprint","IMPRINT",EDGE,{"disambiguationData":[TD([[subQ5,-1.0]])],"derivedFrom":subQ0}),1.0]])]});}
            var Q6;
            {var subQ0=sQuery(id+"F5.wireOp",EDGE,"E21.0");var subQ1=sQuery(id+"F3.wireOp",EDGE,"E14.right");var subQ4=makeQuery(id+"F4.opExtrude","CAP_EDGE",EDGE,{"disambiguationData":[OSD([subQ1])],"isStart":true});var subQ5=makeQuery(id+"F5.imprint","INTERSECT",VERTEX,{"derivedFrom":[subQ4,subQ0]});Q6=makeQuery(id+"F5.imprint","IMPRINT",FACE,{"disambiguationData":[TD([[makeQuery(id+"F5.imprint","IMPRINT",EDGE,{"disambiguationData":[TD([[subQ5,-1.0]])],"derivedFrom":subQ0}),1.0]])]});}
            var Q7;
            {var subQ0=sQuery(id+"F5.wireOp",EDGE,"E21.0");var subQ1=sQuery(id+"F3.wireOp",EDGE,"E14.right");var subQ4=makeQuery(id+"F4.opExtrude","CAP_EDGE",EDGE,{"disambiguationData":[OSD([subQ1])],"isStart":true});var subQ5=makeQuery(id+"F5.imprint","INTERSECT",VERTEX,{"derivedFrom":[subQ4,subQ0]});Q7=makeQuery(id+"F5.imprint","IMPRINT",FACE,{"disambiguationData":[TD([[makeQuery(id+"F5.imprint","IMPRINT",EDGE,{"disambiguationData":[TD([[subQ5,1.0]])],"derivedFrom":subQ0}),1.0]])]});}
            extrude(context, id + "F7", {"entities" : qUnion([Q0, Q1, Q2, Q3, Q4, Q5, Q6, Q7]), "operationType" : NewBodyOperationType.ADD, "oppositeDirection" : true, "depth" : 3 / 101.6 * mm, "offsetDistance" : 25.4 * mm});
        }
        {
            var Q0;
            Q0=makeQuery(id+"F5.imprint","IMPRINT",FACE,{"disambiguationData":[TD([[makeQuery(id+"F5.imprint","IMPRINT",EDGE,{"derivedFrom":sQuery(id+"F5.wireOp",EDGE,"E23.sketch_text.stroke-0")}),-1.0]])]});
            extrude(context, id + "F8", {"entities" : qUnion([Q0]), "operationType" : NewBodyOperationType.REMOVE, "oppositeDirection" : true, "depth" : 1 / 812.8 * mm, "offsetDistance" : 25.4 * mm});
        }
    });
